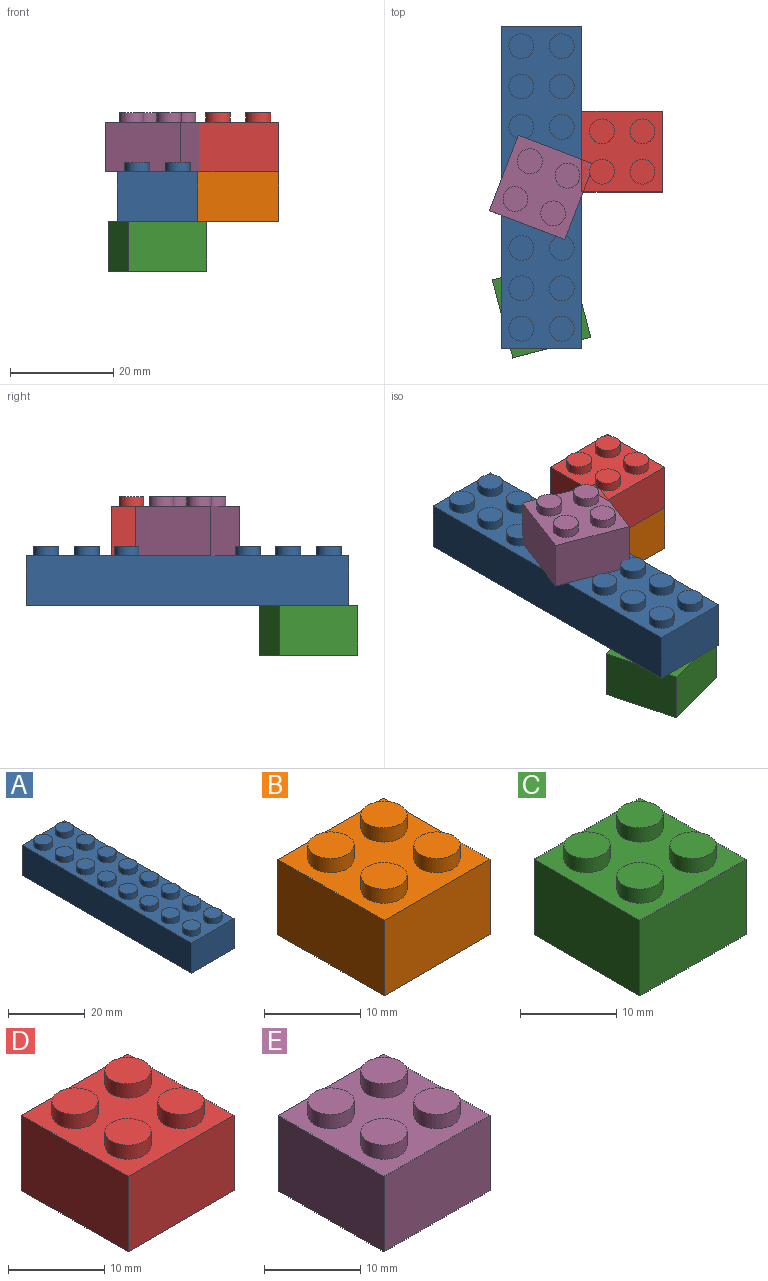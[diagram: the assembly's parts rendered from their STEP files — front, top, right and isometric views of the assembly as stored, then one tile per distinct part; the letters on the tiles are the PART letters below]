
ASSEMBLY  parts=5 mates=5
PART A: 103 faces, bbox 15.6x62.4x11.4 mm
  f0: cylinder r=1.4mm len=2.8mm, axis (0,0,1), area 7.9mm2, adj f26,f72
  f1: cylinder r=1.4mm len=2.8mm, axis (0,0,1), area 7.9mm2, adj f26,f69
  f2: cylinder r=1.4mm len=2.8mm, axis (0,0,1), area 7.9mm2, adj f26,f66
  f3: cylinder r=1.4mm len=2.8mm, axis (0,0,1), area 7.9mm2, adj f26,f63
  f4: cylinder r=1.4mm len=2.8mm, axis (0,0,1), area 7.9mm2, adj f26,f60
  f5: cylinder r=1.4mm len=2.8mm, axis (0,0,1), area 7.9mm2, adj f26,f57
  f6: cylinder r=1.4mm len=2.8mm, axis (0,0,1), area 7.9mm2, adj f26,f54
  f7: cylinder r=1.4mm len=2.8mm, axis (0,0,1), area 7.9mm2, adj f26,f51
  f8: cylinder r=1.4mm len=2.8mm, axis (0,0,1), area 7.9mm2, adj f26,f48
  f9: cylinder r=1.4mm len=2.8mm, axis (0,0,1), area 7.9mm2, adj f26,f45
  f10: cylinder r=1.4mm len=2.8mm, axis (0,0,1), area 7.9mm2, adj f26,f42
  f11: cylinder r=1.4mm len=2.8mm, axis (0,0,1), area 7.9mm2, adj f26,f39
  f12: cylinder r=1.4mm len=2.8mm, axis (0,0,1), area 7.9mm2, adj f26,f36
  f13: cylinder r=1.4mm len=2.8mm, axis (0,0,1), area 7.9mm2, adj f26,f33
  f14: cylinder r=1.4mm len=2.8mm, axis (0,0,1), area 7.9mm2, adj f26,f30
  f15: cylinder r=1.4mm len=2.8mm, axis (0,0,1), area 7.9mm2, adj f26,f27
  f16: plane 62.4x15.6mm, normal (0,0,-1), area 210.6mm2, adj f17,f18,f19,f20,f22,f23,f24,f25
  f17: plane 15.6x9.6mm, normal (0,1,0), area 149.8mm2, adj f16,f18,f20,f21
  f18: plane 62.4x9.6mm, normal (-1,0,0), area 599mm2, adj f16,f17,f19,f21
  f19: plane 15.6x9.6mm, normal (0,-1,0), area 149.8mm2, adj f16,f18,f20,f21
  f20: plane 62.4x9.6mm, normal (1,0,0), area 599mm2, adj f16,f17,f19,f21
  f21: plane 62.4x15.6mm, normal (0,0,1), area 683.9mm2, adj f17,f18,f19,f20,f28,f31,f34,f37
  f22: plane 12.8x8.2mm, normal (0,-1,0), area 105mm2, adj f16,f23,f25,f26
  f23: plane 59.6x8.2mm, normal (1,0,0), area 488.7mm2, adj f16,f22,f24,f26
  f24: plane 12.8x8.2mm, normal (0,1,0), area 105mm2, adj f16,f23,f25,f26
  f25: plane 59.6x8.2mm, normal (-1,0,0), area 488.7mm2, adj f16,f22,f24,f26
  f26: plane 59.6x12.8mm, normal (0,0,-1), area 466.4mm2, adj f0,f1,f2,f3,f4,f5,f6,f7
  f27: plane 2.8x2.8mm, normal (0,0,-1), area 6.2mm2, adj f15
  f28: cylinder r=2.4mm len=4.8mm, axis (0,0,-1), area 27.1mm2, adj f21,f29
  f29: plane 4.8x4.8mm, normal (0,0,1), area 18.1mm2, adj f28
  f30: plane 2.8x2.8mm, normal (0,0,-1), area 6.2mm2, adj f14
  f31: cylinder r=2.4mm len=4.8mm, axis (0,0,-1), area 27.1mm2, adj f21,f32
  f32: plane 4.8x4.8mm, normal (0,0,1), area 18.1mm2, adj f31
  f33: plane 2.8x2.8mm, normal (0,0,-1), area 6.2mm2, adj f13
  f34: cylinder r=2.4mm len=4.8mm, axis (0,0,-1), area 27.1mm2, adj f21,f35
  f35: plane 4.8x4.8mm, normal (0,0,1), area 18.1mm2, adj f34
  f36: plane 2.8x2.8mm, normal (0,0,-1), area 6.2mm2, adj f12
  f37: cylinder r=2.4mm len=4.8mm, axis (0,0,-1), area 27.1mm2, adj f21,f38
  f38: plane 4.8x4.8mm, normal (0,0,1), area 18.1mm2, adj f37
  f39: plane 2.8x2.8mm, normal (0,0,-1), area 6.2mm2, adj f11
  f40: cylinder r=2.4mm len=4.8mm, axis (0,0,-1), area 27.1mm2, adj f21,f41
  f41: plane 4.8x4.8mm, normal (0,0,1), area 18.1mm2, adj f40
  f42: plane 2.8x2.8mm, normal (0,0,-1), area 6.2mm2, adj f10
  f43: cylinder r=2.4mm len=4.8mm, axis (0,0,-1), area 27.1mm2, adj f21,f44
  f44: plane 4.8x4.8mm, normal (0,0,1), area 18.1mm2, adj f43
  f45: plane 2.8x2.8mm, normal (0,0,-1), area 6.2mm2, adj f9
  f46: cylinder r=2.4mm len=4.8mm, axis (0,0,-1), area 27.1mm2, adj f21,f47
  f47: plane 4.8x4.8mm, normal (0,0,1), area 18.1mm2, adj f46
  f48: plane 2.8x2.8mm, normal (0,0,-1), area 6.2mm2, adj f8
  f49: cylinder r=2.4mm len=4.8mm, axis (0,0,-1), area 27.1mm2, adj f21,f50
  f50: plane 4.8x4.8mm, normal (0,0,1), area 18.1mm2, adj f49
  f51: plane 2.8x2.8mm, normal (0,0,-1), area 6.2mm2, adj f7
  f52: cylinder r=2.4mm len=4.8mm, axis (0,0,-1), area 27.1mm2, adj f21,f53
  f53: plane 4.8x4.8mm, normal (0,0,1), area 18.1mm2, adj f52
  f54: plane 2.8x2.8mm, normal (0,0,-1), area 6.2mm2, adj f6
  f55: cylinder r=2.4mm len=4.8mm, axis (0,0,-1), area 27.1mm2, adj f21,f56
  f56: plane 4.8x4.8mm, normal (0,0,1), area 18.1mm2, adj f55
  f57: plane 2.8x2.8mm, normal (0,0,-1), area 6.2mm2, adj f5
  f58: cylinder r=2.4mm len=4.8mm, axis (0,0,-1), area 27.1mm2, adj f21,f59
  f59: plane 4.8x4.8mm, normal (0,0,1), area 18.1mm2, adj f58
  f60: plane 2.8x2.8mm, normal (0,0,-1), area 6.2mm2, adj f4
  f61: cylinder r=2.4mm len=4.8mm, axis (0,0,-1), area 27.1mm2, adj f21,f62
  f62: plane 4.8x4.8mm, normal (0,0,1), area 18.1mm2, adj f61
  f63: plane 2.8x2.8mm, normal (0,0,-1), area 6.2mm2, adj f3
  f64: cylinder r=2.4mm len=4.8mm, axis (0,0,-1), area 27.1mm2, adj f21,f65
  f65: plane 4.8x4.8mm, normal (0,0,1), area 18.1mm2, adj f64
  f66: plane 2.8x2.8mm, normal (0,0,-1), area 6.2mm2, adj f2
  f67: cylinder r=2.4mm len=4.8mm, axis (0,0,-1), area 27.1mm2, adj f21,f68
  f68: plane 4.8x4.8mm, normal (0,0,1), area 18.1mm2, adj f67
  f69: plane 2.8x2.8mm, normal (0,0,-1), area 6.2mm2, adj f1
  f70: cylinder r=2.4mm len=4.8mm, axis (0,0,-1), area 27.1mm2, adj f21,f71
  f71: plane 4.8x4.8mm, normal (0,0,1), area 18.1mm2, adj f70
  f72: plane 2.8x2.8mm, normal (0,0,-1), area 6.2mm2, adj f0
  f73: cylinder r=2.4mm len=4.8mm, axis (0,0,-1), area 27.1mm2, adj f21,f74
  f74: plane 4.8x4.8mm, normal (0,0,1), area 18.1mm2, adj f73
  f75: cylinder r=2.5mm len=8.2mm, axis (0,0,1), area 128.8mm2, adj f77,f78
  f76: cylinder r=3mm len=8.2mm, axis (0,0,1), area 154.6mm2, adj f26,f77
  f77: plane 6x6mm, normal (0,0,-1), area 8.6mm2, adj f75,f76
  f78: plane 5x5mm, normal (0,0,-1), area 19.6mm2, adj f75
  f79: cylinder r=2.5mm len=8.2mm, axis (0,0,1), area 128.8mm2, adj f81,f82
  f80: cylinder r=3mm len=8.2mm, axis (0,0,1), area 154.6mm2, adj f26,f81
  f81: plane 6x6mm, normal (0,0,-1), area 8.6mm2, adj f79,f80
  f82: plane 5x5mm, normal (0,0,-1), area 19.6mm2, adj f79
  f83: cylinder r=2.5mm len=8.2mm, axis (0,0,1), area 128.8mm2, adj f85,f86
  f84: cylinder r=3mm len=8.2mm, axis (0,0,1), area 154.6mm2, adj f26,f85
  f85: plane 6x6mm, normal (0,0,-1), area 8.6mm2, adj f83,f84
  f86: plane 5x5mm, normal (0,0,-1), area 19.6mm2, adj f83
  f87: cylinder r=2.5mm len=8.2mm, axis (0,0,1), area 128.8mm2, adj f89,f90
  f88: cylinder r=3mm len=8.2mm, axis (0,0,1), area 154.6mm2, adj f26,f89
  f89: plane 6x6mm, normal (0,0,-1), area 8.6mm2, adj f87,f88
  f90: plane 5x5mm, normal (0,0,-1), area 19.6mm2, adj f87
  f91: cylinder r=2.5mm len=8.2mm, axis (0,0,1), area 128.8mm2, adj f93,f94
  f92: cylinder r=3mm len=8.2mm, axis (0,0,1), area 154.6mm2, adj f26,f93
  f93: plane 6x6mm, normal (0,0,-1), area 8.6mm2, adj f91,f92
  f94: plane 5x5mm, normal (0,0,-1), area 19.6mm2, adj f91
  f95: cylinder r=2.5mm len=8.2mm, axis (0,0,1), area 128.8mm2, adj f97,f98
  f96: cylinder r=3mm len=8.2mm, axis (0,0,1), area 154.6mm2, adj f26,f97
  f97: plane 6x6mm, normal (0,0,-1), area 8.6mm2, adj f95,f96
  f98: plane 5x5mm, normal (0,0,-1), area 19.6mm2, adj f95
  f99: cylinder r=2.5mm len=8.2mm, axis (0,0,1), area 128.8mm2, adj f101,f102
  f100: cylinder r=3mm len=8.2mm, axis (0,0,1), area 154.6mm2, adj f26,f101
  f101: plane 6x6mm, normal (0,0,-1), area 8.6mm2, adj f99,f100
  f102: plane 5x5mm, normal (0,0,-1), area 19.6mm2, adj f99
PART B: 31 faces, bbox 15.6x15.6x11.4 mm
  f0: cylinder r=1.4mm len=2.8mm, axis (0,0,1), area 7.9mm2, adj f14,f24
  f1: cylinder r=1.4mm len=2.8mm, axis (0,0,1), area 7.9mm2, adj f14,f21
  f2: cylinder r=1.4mm len=2.8mm, axis (0,0,1), area 7.9mm2, adj f14,f18
  f3: cylinder r=1.4mm len=2.8mm, axis (0,0,1), area 7.9mm2, adj f14,f15
  f4: plane 15.6x15.6mm, normal (0,0,-1), area 79.5mm2, adj f5,f6,f7,f8,f10,f11,f12,f13
  f5: plane 15.6x9.6mm, normal (0,1,0), area 149.8mm2, adj f4,f6,f8,f9
  f6: plane 15.6x9.6mm, normal (-1,0,0), area 149.8mm2, adj f4,f5,f7,f9
  f7: plane 15.6x9.6mm, normal (0,-1,0), area 149.8mm2, adj f4,f6,f8,f9
  f8: plane 15.6x9.6mm, normal (1,0,0), area 149.8mm2, adj f4,f5,f7,f9
  f9: plane 15.6x15.6mm, normal (0,0,1), area 171mm2, adj f5,f6,f7,f8,f16,f19,f22,f25
  f10: plane 12.8x8.2mm, normal (0,-1,0), area 105mm2, adj f4,f11,f13,f14
  f11: plane 12.8x8.2mm, normal (1,0,0), area 105mm2, adj f4,f10,f12,f14
  f12: plane 12.8x8.2mm, normal (0,1,0), area 105mm2, adj f4,f11,f13,f14
  f13: plane 12.8x8.2mm, normal (-1,0,0), area 105mm2, adj f4,f10,f12,f14
  f14: plane 12.8x12.8mm, normal (0,0,-1), area 110.9mm2, adj f0,f1,f2,f3,f10,f11,f12,f13
  f15: plane 2.8x2.8mm, normal (0,0,-1), area 6.2mm2, adj f3
  f16: cylinder r=2.4mm len=4.8mm, axis (0,0,-1), area 27.1mm2, adj f9,f17
  f17: plane 4.8x4.8mm, normal (0,0,1), area 18.1mm2, adj f16
  f18: plane 2.8x2.8mm, normal (0,0,-1), area 6.2mm2, adj f2
  f19: cylinder r=2.4mm len=4.8mm, axis (0,0,-1), area 27.1mm2, adj f9,f20
  f20: plane 4.8x4.8mm, normal (0,0,1), area 18.1mm2, adj f19
  f21: plane 2.8x2.8mm, normal (0,0,-1), area 6.2mm2, adj f1
  f22: cylinder r=2.4mm len=4.8mm, axis (0,0,-1), area 27.1mm2, adj f9,f23
  f23: plane 4.8x4.8mm, normal (0,0,1), area 18.1mm2, adj f22
  f24: plane 2.8x2.8mm, normal (0,0,-1), area 6.2mm2, adj f0
  f25: cylinder r=2.4mm len=4.8mm, axis (0,0,-1), area 27.1mm2, adj f9,f26
  f26: plane 4.8x4.8mm, normal (0,0,1), area 18.1mm2, adj f25
  f27: cylinder r=2.5mm len=8.2mm, axis (0,0,1), area 128.8mm2, adj f29,f30
  f28: cylinder r=3mm len=8.2mm, axis (0,0,1), area 154.6mm2, adj f14,f29
  f29: plane 6x6mm, normal (0,0,-1), area 8.6mm2, adj f27,f28
  f30: plane 5x5mm, normal (0,0,-1), area 19.6mm2, adj f27
PART C: 31 faces, bbox 15.6x15.6x11.4 mm
  f0: cylinder r=1.4mm len=2.8mm, axis (0,0,1), area 7.9mm2, adj f14,f24
  f1: cylinder r=1.4mm len=2.8mm, axis (0,0,1), area 7.9mm2, adj f14,f21
  f2: cylinder r=1.4mm len=2.8mm, axis (0,0,1), area 7.9mm2, adj f14,f18
  f3: cylinder r=1.4mm len=2.8mm, axis (0,0,1), area 7.9mm2, adj f14,f15
  f4: plane 15.6x15.6mm, normal (0,0,-1), area 79.5mm2, adj f5,f6,f7,f8,f10,f11,f12,f13
  f5: plane 15.6x9.6mm, normal (0,1,0), area 149.8mm2, adj f4,f6,f8,f9
  f6: plane 15.6x9.6mm, normal (-1,0,0), area 149.8mm2, adj f4,f5,f7,f9
  f7: plane 15.6x9.6mm, normal (0,-1,0), area 149.8mm2, adj f4,f6,f8,f9
  f8: plane 15.6x9.6mm, normal (1,0,0), area 149.8mm2, adj f4,f5,f7,f9
  f9: plane 15.6x15.6mm, normal (0,0,1), area 171mm2, adj f5,f6,f7,f8,f16,f19,f22,f25
  f10: plane 12.8x8.2mm, normal (0,-1,0), area 105mm2, adj f4,f11,f13,f14
  f11: plane 12.8x8.2mm, normal (1,0,0), area 105mm2, adj f4,f10,f12,f14
  f12: plane 12.8x8.2mm, normal (0,1,0), area 105mm2, adj f4,f11,f13,f14
  f13: plane 12.8x8.2mm, normal (-1,0,0), area 105mm2, adj f4,f10,f12,f14
  f14: plane 12.8x12.8mm, normal (0,0,-1), area 110.9mm2, adj f0,f1,f2,f3,f10,f11,f12,f13
  f15: plane 2.8x2.8mm, normal (0,0,-1), area 6.2mm2, adj f3
  f16: cylinder r=2.4mm len=4.8mm, axis (0,0,-1), area 27.1mm2, adj f9,f17
  f17: plane 4.8x4.8mm, normal (0,0,1), area 18.1mm2, adj f16
  f18: plane 2.8x2.8mm, normal (0,0,-1), area 6.2mm2, adj f2
  f19: cylinder r=2.4mm len=4.8mm, axis (0,0,-1), area 27.1mm2, adj f9,f20
  f20: plane 4.8x4.8mm, normal (0,0,1), area 18.1mm2, adj f19
  f21: plane 2.8x2.8mm, normal (0,0,-1), area 6.2mm2, adj f1
  f22: cylinder r=2.4mm len=4.8mm, axis (0,0,-1), area 27.1mm2, adj f9,f23
  f23: plane 4.8x4.8mm, normal (0,0,1), area 18.1mm2, adj f22
  f24: plane 2.8x2.8mm, normal (0,0,-1), area 6.2mm2, adj f0
  f25: cylinder r=2.4mm len=4.8mm, axis (0,0,-1), area 27.1mm2, adj f9,f26
  f26: plane 4.8x4.8mm, normal (0,0,1), area 18.1mm2, adj f25
  f27: cylinder r=2.5mm len=8.2mm, axis (0,0,1), area 128.8mm2, adj f29,f30
  f28: cylinder r=3mm len=8.2mm, axis (0,0,1), area 154.6mm2, adj f14,f29
  f29: plane 6x6mm, normal (0,0,-1), area 8.6mm2, adj f27,f28
  f30: plane 5x5mm, normal (0,0,-1), area 19.6mm2, adj f27
PART D: 31 faces, bbox 15.6x15.6x11.4 mm
  f0: cylinder r=1.4mm len=2.8mm, axis (0,0,1), area 7.9mm2, adj f14,f24
  f1: cylinder r=1.4mm len=2.8mm, axis (0,0,1), area 7.9mm2, adj f14,f21
  f2: cylinder r=1.4mm len=2.8mm, axis (0,0,1), area 7.9mm2, adj f14,f18
  f3: cylinder r=1.4mm len=2.8mm, axis (0,0,1), area 7.9mm2, adj f14,f15
  f4: plane 15.6x15.6mm, normal (0,0,-1), area 79.5mm2, adj f5,f6,f7,f8,f10,f11,f12,f13
  f5: plane 15.6x9.6mm, normal (0,1,0), area 149.8mm2, adj f4,f6,f8,f9
  f6: plane 15.6x9.6mm, normal (-1,0,0), area 149.8mm2, adj f4,f5,f7,f9
  f7: plane 15.6x9.6mm, normal (0,-1,0), area 149.8mm2, adj f4,f6,f8,f9
  f8: plane 15.6x9.6mm, normal (1,0,0), area 149.8mm2, adj f4,f5,f7,f9
  f9: plane 15.6x15.6mm, normal (0,0,1), area 171mm2, adj f5,f6,f7,f8,f16,f19,f22,f25
  f10: plane 12.8x8.2mm, normal (0,-1,0), area 105mm2, adj f4,f11,f13,f14
  f11: plane 12.8x8.2mm, normal (1,0,0), area 105mm2, adj f4,f10,f12,f14
  f12: plane 12.8x8.2mm, normal (0,1,0), area 105mm2, adj f4,f11,f13,f14
  f13: plane 12.8x8.2mm, normal (-1,0,0), area 105mm2, adj f4,f10,f12,f14
  f14: plane 12.8x12.8mm, normal (0,0,-1), area 110.9mm2, adj f0,f1,f2,f3,f10,f11,f12,f13
  f15: plane 2.8x2.8mm, normal (0,0,-1), area 6.2mm2, adj f3
  f16: cylinder r=2.4mm len=4.8mm, axis (0,0,-1), area 27.1mm2, adj f9,f17
  f17: plane 4.8x4.8mm, normal (0,0,1), area 18.1mm2, adj f16
  f18: plane 2.8x2.8mm, normal (0,0,-1), area 6.2mm2, adj f2
  f19: cylinder r=2.4mm len=4.8mm, axis (0,0,-1), area 27.1mm2, adj f9,f20
  f20: plane 4.8x4.8mm, normal (0,0,1), area 18.1mm2, adj f19
  f21: plane 2.8x2.8mm, normal (0,0,-1), area 6.2mm2, adj f1
  f22: cylinder r=2.4mm len=4.8mm, axis (0,0,-1), area 27.1mm2, adj f9,f23
  f23: plane 4.8x4.8mm, normal (0,0,1), area 18.1mm2, adj f22
  f24: plane 2.8x2.8mm, normal (0,0,-1), area 6.2mm2, adj f0
  f25: cylinder r=2.4mm len=4.8mm, axis (0,0,-1), area 27.1mm2, adj f9,f26
  f26: plane 4.8x4.8mm, normal (0,0,1), area 18.1mm2, adj f25
  f27: cylinder r=2.5mm len=8.2mm, axis (0,0,1), area 128.8mm2, adj f29,f30
  f28: cylinder r=3mm len=8.2mm, axis (0,0,1), area 154.6mm2, adj f14,f29
  f29: plane 6x6mm, normal (0,0,-1), area 8.6mm2, adj f27,f28
  f30: plane 5x5mm, normal (0,0,-1), area 19.6mm2, adj f27
PART E: 31 faces, bbox 15.6x15.6x11.4 mm
  f0: cylinder r=1.4mm len=2.8mm, axis (0,0,1), area 7.9mm2, adj f14,f24
  f1: cylinder r=1.4mm len=2.8mm, axis (0,0,1), area 7.9mm2, adj f14,f21
  f2: cylinder r=1.4mm len=2.8mm, axis (0,0,1), area 7.9mm2, adj f14,f18
  f3: cylinder r=1.4mm len=2.8mm, axis (0,0,1), area 7.9mm2, adj f14,f15
  f4: plane 15.6x15.6mm, normal (0,0,-1), area 79.5mm2, adj f5,f6,f7,f8,f10,f11,f12,f13
  f5: plane 15.6x9.6mm, normal (0,1,0), area 149.8mm2, adj f4,f6,f8,f9
  f6: plane 15.6x9.6mm, normal (-1,0,0), area 149.8mm2, adj f4,f5,f7,f9
  f7: plane 15.6x9.6mm, normal (0,-1,0), area 149.8mm2, adj f4,f6,f8,f9
  f8: plane 15.6x9.6mm, normal (1,0,0), area 149.8mm2, adj f4,f5,f7,f9
  f9: plane 15.6x15.6mm, normal (0,0,1), area 171mm2, adj f5,f6,f7,f8,f16,f19,f22,f25
  f10: plane 12.8x8.2mm, normal (0,-1,0), area 105mm2, adj f4,f11,f13,f14
  f11: plane 12.8x8.2mm, normal (1,0,0), area 105mm2, adj f4,f10,f12,f14
  f12: plane 12.8x8.2mm, normal (0,1,0), area 105mm2, adj f4,f11,f13,f14
  f13: plane 12.8x8.2mm, normal (-1,0,0), area 105mm2, adj f4,f10,f12,f14
  f14: plane 12.8x12.8mm, normal (0,0,-1), area 110.9mm2, adj f0,f1,f2,f3,f10,f11,f12,f13
  f15: plane 2.8x2.8mm, normal (0,0,-1), area 6.2mm2, adj f3
  f16: cylinder r=2.4mm len=4.8mm, axis (0,0,-1), area 27.1mm2, adj f9,f17
  f17: plane 4.8x4.8mm, normal (0,0,1), area 18.1mm2, adj f16
  f18: plane 2.8x2.8mm, normal (0,0,-1), area 6.2mm2, adj f2
  f19: cylinder r=2.4mm len=4.8mm, axis (0,0,-1), area 27.1mm2, adj f9,f20
  f20: plane 4.8x4.8mm, normal (0,0,1), area 18.1mm2, adj f19
  f21: plane 2.8x2.8mm, normal (0,0,-1), area 6.2mm2, adj f1
  f22: cylinder r=2.4mm len=4.8mm, axis (0,0,-1), area 27.1mm2, adj f9,f23
  f23: plane 4.8x4.8mm, normal (0,0,1), area 18.1mm2, adj f22
  f24: plane 2.8x2.8mm, normal (0,0,-1), area 6.2mm2, adj f0
  f25: cylinder r=2.4mm len=4.8mm, axis (0,0,-1), area 27.1mm2, adj f9,f26
  f26: plane 4.8x4.8mm, normal (0,0,1), area 18.1mm2, adj f25
  f27: cylinder r=2.5mm len=8.2mm, axis (0,0,1), area 128.8mm2, adj f29,f30
  f28: cylinder r=3mm len=8.2mm, axis (0,0,1), area 154.6mm2, adj f14,f29
  f29: plane 6x6mm, normal (0,0,-1), area 8.6mm2, adj f27,f28
  f30: plane 5x5mm, normal (0,0,-1), area 19.6mm2, adj f27
PLACE A t=(0.62,8.18,8.94)mm fixed
PLACE B rot(axis=(0,0,1),90deg) t=(81.82,21.51,8.94)mm
PLACE C rot(axis=(0,0,-1),165.2deg) t=(-2.47,21.17,-0.66)mm
PLACE D rot(axis=(0,0,1),90deg) t=(81.82,55.51,18.54)mm
PLACE E rot(axis=(0,0,1),159.1deg) t=(34.37,37.83,18.54)mm
MATE fastened B.f27 <-> D.f27  axis (0,0,1) through (24.02,46.31,18.54)mm
MATE revolute A.f75 <-> C.f27  axis (0,0,-1) through (8.42,15.98,8.94)mm
MATE planar A.f20 <-> D.f5  axis (1,0,0) through (16.22,70.58,13.74)mm
MATE revolute E.f27 <-> A.f87  axis (0,0,-1) through (8.42,39.38,18.54)mm
MATE slider A.f17 <-> B.f8  axis (0,-1,0) through (16.22,70.58,8.94)mm
